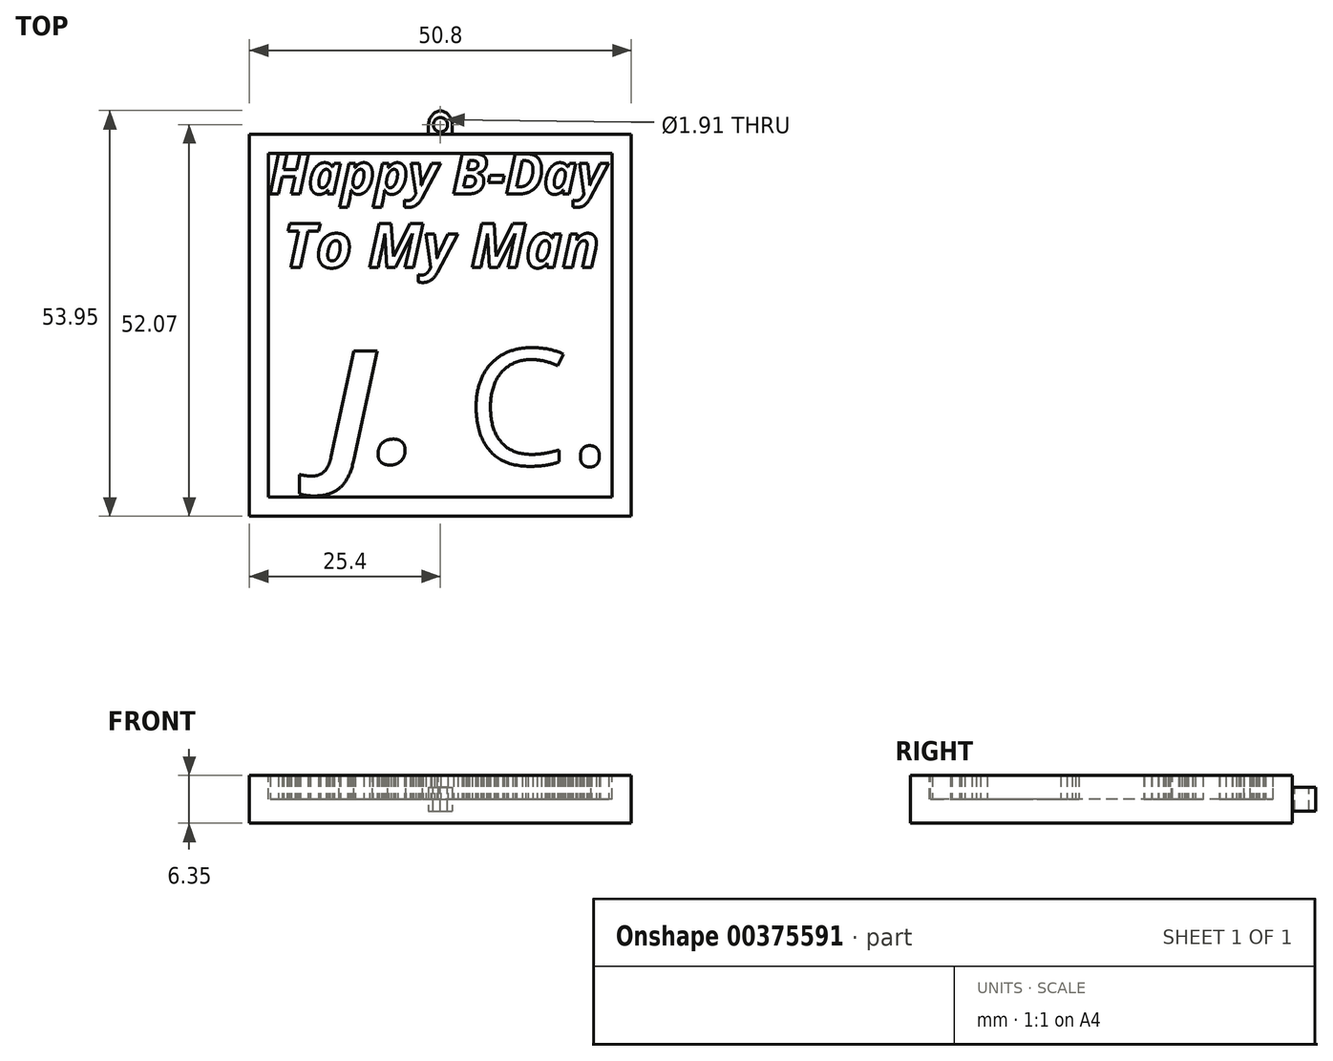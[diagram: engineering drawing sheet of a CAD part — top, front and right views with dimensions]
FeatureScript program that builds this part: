
annotation { "Feature Type Name" : "Feature", "Feature Type Description" : "" }
export const myFeature = defineFeature(function(context is Context, id is Id, definition is map)
    precondition{}
    {
        {
            var Q0;
            Q0=qCreatedBy(makeId("Top.planeOp"),FACE);
            var sketch = newSketch(context, id + "F0", { "sketchPlane" : qUnion([Q0])});
            skLineSegment(sketch, "E0.bottom", {"start": v(25.4, 25.4) * mm, "end": v(-25.4, 25.4) * mm});
            skLineSegment(sketch, "E0.top", {"start": v(25.4, -25.4) * mm, "end": v(-25.4, -25.4) * mm});
            skLineSegment(sketch, "E0.left", {"start": v(25.4, 25.4) * mm, "end": v(25.4, -25.4) * mm});
            skLineSegment(sketch, "E0.right", {"start": v(-25.4, 25.4) * mm, "end": v(-25.4, -25.4) * mm});
            skPoint(sketch, "E0.middle", {"position": v(0, 0) * mm});
            skSolve(sketch);
        }
        {
            var Q0;
            Q0=makeQuery(id+"F0.imprint","IMPRINT",FACE,{"disambiguationData":[TD([[makeQuery(id+"F0.imprint","IMPRINT",EDGE,{"derivedFrom":sQuery(id+"F0.wireOp",EDGE,"E0.bottom")}),1.0]])]});
            extrude(context, id + "F1", {"entities" : qUnion([Q0]), "depth" : 6.35 * mm});
        }
        {
            var Q0;
            Q0=makeQuery(id+"F1.opExtrude","CAP_FACE",FACE,{"disambiguationData":[OSD([sQuery(id+"F0.wireOp",EDGE,"E0.bottom"),sQuery(id+"F0.wireOp",EDGE,"E0.top"),sQuery(id+"F0.wireOp",EDGE,"E0.left"),sQuery(id+"F0.wireOp",EDGE,"E0.right")])],"isStart":false});
            var sketch = newSketch(context, id + "F2", { "sketchPlane" : qUnion([Q0])});
            skLineSegment(sketch, "E1.bottom", {"start": v(22.86, 22.86) * mm, "end": v(-22.86, 22.86) * mm});
            skLineSegment(sketch, "E1.top", {"start": v(22.86, -22.86) * mm, "end": v(-22.86, -22.86) * mm});
            skLineSegment(sketch, "E1.left", {"start": v(22.86, 22.86) * mm, "end": v(22.86, -22.86) * mm});
            skLineSegment(sketch, "E1.right", {"start": v(-22.86, 22.86) * mm, "end": v(-22.86, -22.86) * mm});
            skPoint(sketch, "E1.middle", {"position": v(0, 0) * mm});
            skSolve(sketch);
        }
        {
            var Q0;
            Q0=makeQuery(id+"F2.imprint","IMPRINT",FACE,{"disambiguationData":[TD([[makeQuery(id+"F2.imprint","IMPRINT",EDGE,{"derivedFrom":sQuery(id+"F2.wireOp",EDGE,"E1.bottom")}),1.0]])]});
            extrude(context, id + "F3", {"entities" : qUnion([Q0]), "operationType" : NewBodyOperationType.REMOVE, "oppositeDirection" : true, "depth" : 3.17 * mm});
        }
        {
            var Q0;
            Q0=makeQuery(id+"F3.boolean.opBoolean","COPY",FACE,{"derivedFrom":makeQuery(id+"F3.opExtrude","CAP_FACE",FACE,{"disambiguationData":[OSD([sQuery(id+"F2.wireOp",EDGE,"E1.bottom"),sQuery(id+"F2.wireOp",EDGE,"E1.top"),sQuery(id+"F2.wireOp",EDGE,"E1.left"),sQuery(id+"F2.wireOp",EDGE,"E1.right")])],"isStart":false})});
            var sketch = newSketch(context, id + "F4", { "sketchPlane" : qUnion([Q0])});
            skText(sketch, "E2", { "text": "Happy B-Day\n", "fontName": "OpenSans-BoldItalic.ttf"});
            skText(sketch, "E3", { "text": "To My Man\n", "fontName": "OpenSans-BoldItalic.ttf"});
            skText(sketch, "E4", { "text": "J.", "fontName": "OpenSans-BoldItalic.ttf"});
            skText(sketch, "E5", { "text": "C.\n", "fontName": "OpenSans-Regular.ttf"});
            const initialGuessF4  = {"E2": [-0.02286, 0.01747, 1, 0, 0.00539], "E3": [-0.02095, 0.00766, 1, 0, 0.00593], "E4": [-0.01548, -0.01833, 1, 0, 0.01504], "E5": [0.00343, -0.01856, 1, 0, 0.0155]};
            skSetInitialGuess(sketch, initialGuessF4);
            skSolve(sketch);
        }
        {
            var Q0;
            Q0 = qSketchRegion(id + "F4", true);
            var Q1;
            Q1=makeQuery(id+"F1.opExtrude","CAP_FACE",FACE,{"disambiguationData":[OSD([sQuery(id+"F0.wireOp",EDGE,"E0.bottom"),sQuery(id+"F0.wireOp",EDGE,"E0.top"),sQuery(id+"F0.wireOp",EDGE,"E0.left"),sQuery(id+"F0.wireOp",EDGE,"E0.right")])],"isStart":false});
            extrude(context, id + "F5", {"entities" : qUnion([Q0]), "operationType" : NewBodyOperationType.ADD, "endBound" : BoundingType.UP_TO_SURFACE, "endBoundEntityFace" : qUnion([Q1]), "depth" : 25.4 * mm});
        }
        {
            var Q0;
            Q0=makeQuery(id+"F1.opExtrude","SWEPT_FACE",FACE,{"disambiguationData":[OSD([sQuery(id+"F0.wireOp",EDGE,"E0.bottom")])]});
            var sketch = newSketch(context, id + "F6", { "sketchPlane" : qUnion([Q0])});
            skLineSegment(sketch, "E6.bottom", {"start": v(1.59, 4.76) * mm, "end": v(-1.59, 4.76) * mm});
            skLineSegment(sketch, "E6.top", {"start": v(1.59, 1.59) * mm, "end": v(-1.59, 1.59) * mm});
            skLineSegment(sketch, "E6.left", {"start": v(1.59, 4.76) * mm, "end": v(1.59, 1.59) * mm});
            skLineSegment(sketch, "E6.right", {"start": v(-1.59, 4.76) * mm, "end": v(-1.59, 1.59) * mm});
            skPoint(sketch, "E6.middle", {"position": v(0, 3.18) * mm});
            skPoint(sketch, "E6.middle.positionSnap0", {"position": v(-25.4, 3.18) * mm});
            skPoint(sketch, "E6.middle.positionSnap1", {"position": v(0, 6.35) * mm});
            skPoint(sketch, "E6.centerSnap0", {"position": v(-25.4, 3.18) * mm});
            skPoint(sketch, "E6.centerSnap1", {"position": v(0, 6.35) * mm});
            skSolve(sketch);
        }
        {
            var Q0;
            Q0=makeQuery(id+"F6.imprint","IMPRINT",FACE,{"disambiguationData":[TD([[makeQuery(id+"F6.imprint","IMPRINT",EDGE,{"derivedFrom":sQuery(id+"F6.wireOp",EDGE,"E6.bottom")}),1.0]])]});
            extrude(context, id + "F7", {"entities" : qUnion([Q0]), "operationType" : NewBodyOperationType.ADD, "depth" : 3.17 * mm});
        }
        {
            var Q0;
            Q0=makeQuery(id+"F7.opExtrude","CAP_EDGE",EDGE,{"disambiguationData":[OSD([sQuery(id+"F6.wireOp",EDGE,"E6.right")])],"isStart":false});
            var Q1;
            Q1=makeQuery(id+"F7.opExtrude","CAP_EDGE",EDGE,{"disambiguationData":[OSD([sQuery(id+"F6.wireOp",EDGE,"E6.left")])],"isStart":false});
            fillet(context, id + "F8", {"entities" : qUnion([Q0, Q1]), "radius" : 1.9 * mm, "tangentPropagation" : true, "allowEdgeOverflow" : false});
        }
        {
            var Q0;
            Q0=makeQuery(id+"F7.opExtrude","SWEPT_FACE",FACE,{"disambiguationData":[OSD([sQuery(id+"F6.wireOp",EDGE,"E6.bottom")])]});
            var sketch = newSketch(context, id + "F9", { "sketchPlane" : qUnion([Q0])});
            skCircle(sketch, "E7", {"center": v(0, 26.67) * mm, "radius": 0.95 * mm});
            skSolve(sketch);
        }
        {
            var Q0;
            Q0=makeQuery(id+"F9.imprint","IMPRINT",FACE,{"disambiguationData":[TD([[makeQuery(id+"F9.imprint","IMPRINT",EDGE,{"derivedFrom":sQuery(id+"F9.wireOp",EDGE,"E7")}),1.0]])]});
            var Q1;
            Q1=makeQuery(id+"F7.opExtrude","SWEPT_FACE",FACE,{"disambiguationData":[OSD([sQuery(id+"F6.wireOp",EDGE,"E6.top")])]});
            extrude(context, id + "F10", {"entities" : qUnion([Q0]), "operationType" : NewBodyOperationType.REMOVE, "endBound" : BoundingType.UP_TO_SURFACE, "oppositeDirection" : true, "endBoundEntityFace" : qUnion([Q1]), "depth" : 25.4 * mm});
        }
    });
